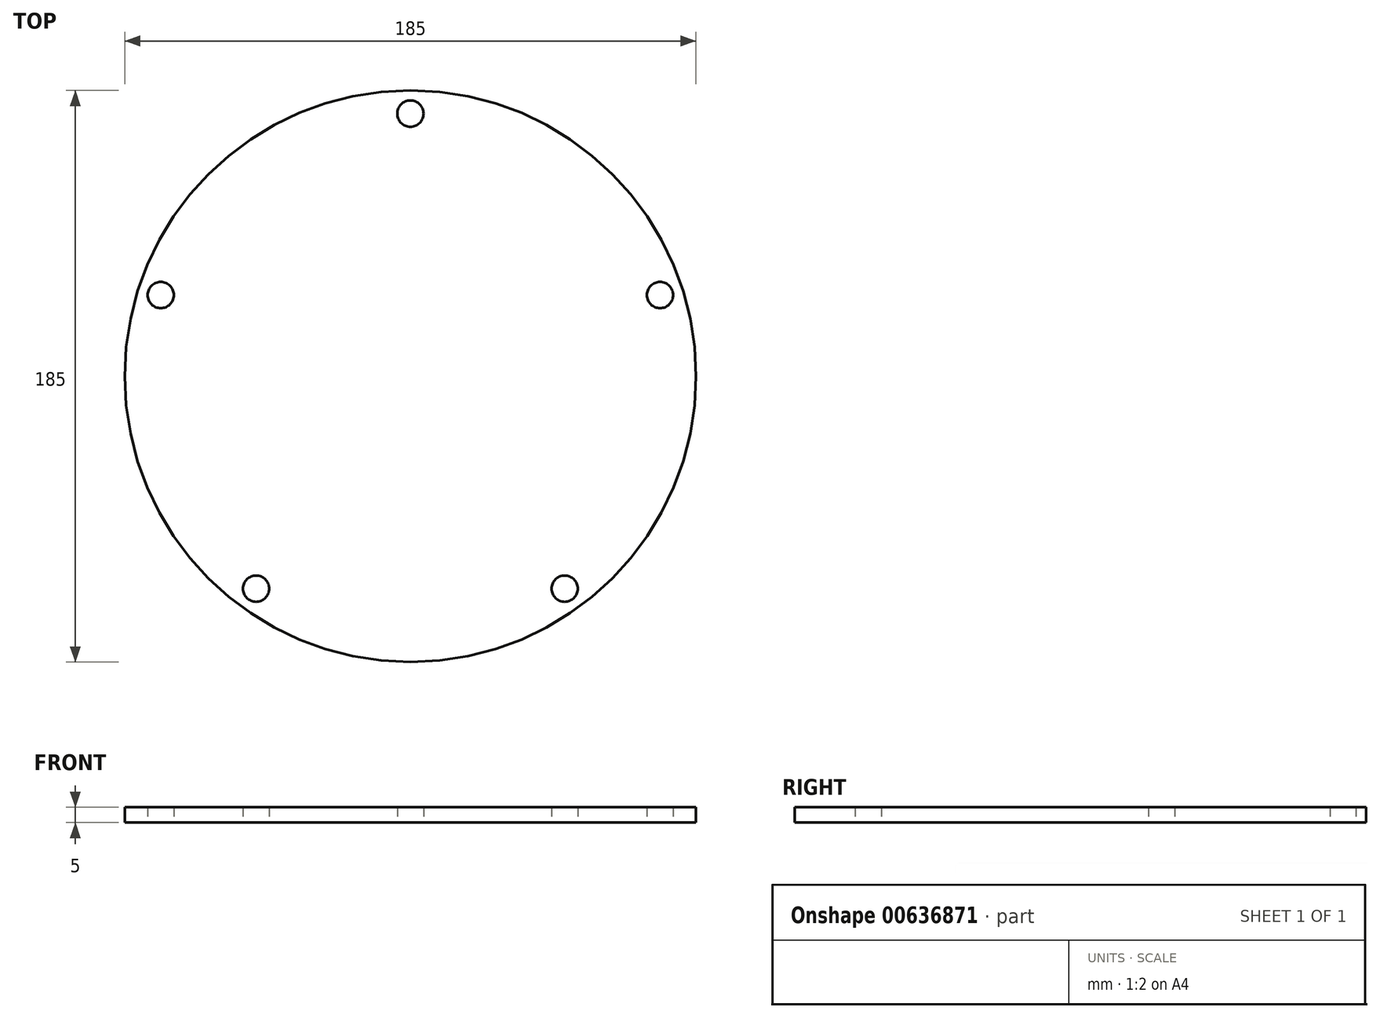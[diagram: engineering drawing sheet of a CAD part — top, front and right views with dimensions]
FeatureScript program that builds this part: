
annotation { "Feature Type Name" : "Feature", "Feature Type Description" : "" }
export const myFeature = defineFeature(function(context is Context, id is Id, definition is map)
    precondition{}
    {
        {
            var Q0;
            Q0=qCreatedBy(makeId("Top.planeOp"),FACE);
            var sketch = newSketch(context, id + "F0", { "sketchPlane" : qUnion([Q0])});
            skCircle(sketch, "E0", {"center": v(0, 0) * mm, "radius": 92.5 * mm});
            skCircle(sketch, "E1", {"center": v(0, 85) * mm, "radius": 4.25 * mm});
            skCircle(sketch, "E2.1.0", {"center": v(-80.84, 26.27) * mm, "radius": 4.25 * mm});
            skCircle(sketch, "E2.2.0", {"center": v(-49.96, -68.77) * mm, "radius": 4.25 * mm});
            skCircle(sketch, "E2.3.0", {"center": v(49.96, -68.77) * mm, "radius": 4.25 * mm});
            skCircle(sketch, "E2.4.0", {"center": v(80.84, 26.27) * mm, "radius": 4.25 * mm});
            skSolve(sketch);
        }
        {
            var Q0;
            Q0=makeQuery(id+"F0.imprint","IMPRINT",FACE,{"disambiguationData":[TD([[makeQuery(id+"F0.imprint","IMPRINT",EDGE,{"derivedFrom":sQuery(id+"F0.wireOp",EDGE,"I694Ymja-XMzd-5B5G-zwoQ-3zzzAEuNOlKW")}),-1.0]])]});
            var Q1;
            Q1=makeQuery(id+"F0.imprint","IMPRINT",FACE,{"disambiguationData":[TD([[makeQuery(id+"F0.imprint","IMPRINT",EDGE,{"derivedFrom":sQuery(id+"F0.wireOp",EDGE,"E0")}),1.0]])]});
            extrude(context, id + "F1", {"entities" : qUnion([Q0, Q1]), "depth" : 5 * mm, "offsetDistance" : 25 * mm});
        }
    });
